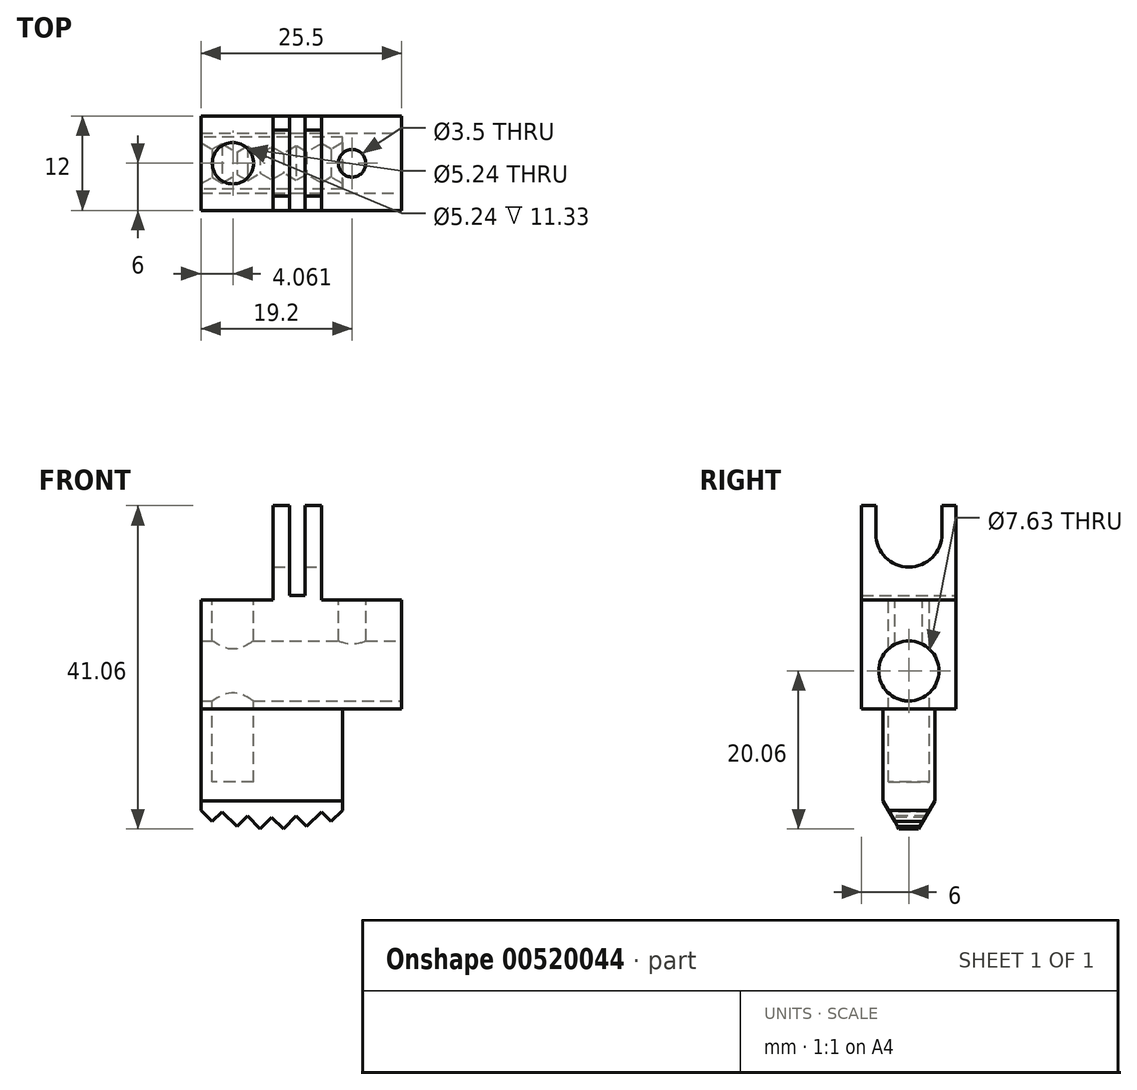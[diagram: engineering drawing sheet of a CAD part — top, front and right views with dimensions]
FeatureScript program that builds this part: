
annotation { "Feature Type Name" : "Feature", "Feature Type Description" : "" }
export const myFeature = defineFeature(function(context is Context, id is Id, definition is map)
    precondition{}
    {
        {
            var Q0;
            Q0=qCreatedBy(makeId("Front.planeOp"),FACE);
            var sketch = newSketch(context, id + "F0", { "sketchPlane" : qUnion([Q0])});
            skLineSegment(sketch, "E0", {"start": v(0, 0) * mm, "end": v(-6, 0) * mm});
            skLineSegment(sketch, "E1", {"start": v(0, 0) * mm, "end": v(0, 5.1) * mm});
            skLineSegment(sketch, "E2", {"start": v(0, 5.1) * mm, "end": v(2.5, 5.1) * mm});
            skLineSegment(sketch, "E3", {"start": v(2.5, 5.1) * mm, "end": v(2.5, 9.7) * mm});
            skLineSegment(sketch, "E4", {"start": v(2.5, 9.7) * mm, "end": v(-0.9, 9.7) * mm});
            skLineSegment(sketch, "E5", {"start": v(-0.9, 9.7) * mm, "end": v(-0.9, 13.7) * mm});
            skLineSegment(sketch, "E6", {"start": v(-0.9, 13.7) * mm, "end": v(-1.6, 13.7) * mm});
            skLineSegment(sketch, "E7", {"start": v(-1.6, 13.7) * mm, "end": v(-1.6, 9.9) * mm});
            skLineSegment(sketch, "E8", {"start": v(-1.6, 9.9) * mm, "end": v(-2.25, 9.9) * mm});
            skLineSegment(sketch, "E9", {"start": v(-2.25, 9.9) * mm, "end": v(-2.25, 13.7) * mm});
            skLineSegment(sketch, "E10", {"start": v(-2.25, 13.7) * mm, "end": v(-2.95, 13.7) * mm});
            skLineSegment(sketch, "E11", {"start": v(-2.95, 13.7) * mm, "end": v(-2.95, 9.7) * mm});
            skLineSegment(sketch, "E12", {"start": v(-2.95, 9.7) * mm, "end": v(-6, 9.7) * mm});
            skLineSegment(sketch, "E13", {"start": v(-6, 9.7) * mm, "end": v(-6, 0) * mm});
            skLineSegment(sketch, "E14", {"start": v(-3, 0) * mm, "end": v(-3, 10) * mm, "construction": true});
            skCircle(sketch, "E15", {"center": v(-3, 10) * mm, "radius": 10 * mm, "construction": true});
            skLineSegment(sketch, "E16", {"start": v(0, 5.1) * mm, "end": v(-6, 5.1) * mm});
            skSolve(sketch);
        }
        {
            var Q0;
            Q0=makeQuery(id+"F0.imprint","IMPRINT",FACE,{"disambiguationData":[TD([[makeQuery(id+"F0.imprint","IMPRINT",EDGE,{"derivedFrom":sQuery(id+"F0.wireOp",EDGE,"E2")}),1.0]])]});
            extrude(context, id + "F1", {"entities" : qUnion([Q0]), "endBound" : BoundingType.SYMMETRIC, "depth" : 4 * mm});
        }
        {
            var Q0;
            {var subQ2=sQuery(id+"F0.wireOp",EDGE,"E0");Q0=makeQuery(id+"F0.imprint","IMPRINT",FACE,{"disambiguationData":[TD([[makeQuery(id+"F0.imprint","IMPRINT",EDGE,{"derivedFrom":subQ2}),-1.0]])]});}
            extrude(context, id + "F2", {"entities" : qUnion([Q0]), "operationType" : NewBodyOperationType.ADD, "endBound" : BoundingType.SYMMETRIC, "depth" : 2.2 * mm});
        }
        {
            var Q0;
            Q0=makeQuery(id+"F1.opExtrude","SWEPT_FACE",FACE,{"disambiguationData":[OSD([sQuery(id+"F0.wireOp",EDGE,"E5")])]});
            var sketch = newSketch(context, id + "F3", { "sketchPlane" : qUnion([Q0])});
            skLineSegment(sketch, "E17", {"start": v(2, 11.1) * mm, "end": v(-2, 11.1) * mm, "construction": true});
            skArc(sketch, "E18", {"start": v(-1.4, 12.5) * mm, "mid": v(0, 11.1) * mm, "end": v(1.4, 12.5) * mm});
            skLineSegment(sketch, "E19", {"start": v(-1.4, 12.5) * mm, "end": v(-1.4, 13.9) * mm});
            skLineSegment(sketch, "E20", {"start": v(-1.4, 13.9) * mm, "end": v(1.4, 13.9) * mm});
            skLineSegment(sketch, "E21", {"start": v(1.4, 13.9) * mm, "end": v(1.4, 12.5) * mm});
            skSolve(sketch);
        }
        {
            var Q0;
            {var subQ5=sQuery(id+"F3.wireOp",EDGE,"E20");Q0=makeQuery(id+"F3.imprint","IMPRINT",FACE,{"disambiguationData":[TD([[makeQuery(id+"F3.imprint","IMPRINT",EDGE,{"derivedFrom":subQ5}),-1.0]])]});}
            var Q1;
            {var subQ5=sQuery(id+"F3.wireOp",EDGE,"E18");Q1=makeQuery(id+"F3.imprint","IMPRINT",FACE,{"disambiguationData":[TD([[makeQuery(id+"F3.imprint","IMPRINT",EDGE,{"derivedFrom":subQ5}),1.0]])]});}
            var Q2;
            Q2=makeQuery(id+"F1.opExtrude","SWEPT_FACE",FACE,{"disambiguationData":[OSD([sQuery(id+"F0.wireOp",EDGE,"E11")])]});
            extrude(context, id + "F4", {"entities" : qUnion([Q0, Q1]), "operationType" : NewBodyOperationType.REMOVE, "endBound" : BoundingType.UP_TO_SURFACE, "oppositeDirection" : true, "endBoundEntityFace" : qUnion([Q2]), "depth" : 2 * mm});
        }
        {
            var Q0;
            Q0=makeQuery(id+"F1.opExtrude","SWEPT_FACE",FACE,{"disambiguationData":[OSD([sQuery(id+"F0.wireOp",EDGE,"E3")])]});
            var sketch = newSketch(context, id + "F5", { "sketchPlane" : qUnion([Q0])});
            skLineSegment(sketch, "E22", {"start": v(0, 9.7) * mm, "end": v(0, 6.7) * mm, "construction": true});
            skCircle(sketch, "E23", {"center": v(0, 6.7) * mm, "radius": 1.27 * mm});
            skSolve(sketch);
        }
        {
            var Q0;
            Q0=makeQuery(id+"F5.imprint","IMPRINT",FACE,{"disambiguationData":[TD([[makeQuery(id+"F5.imprint","IMPRINT",EDGE,{"derivedFrom":sQuery(id+"F5.wireOp",EDGE,"E23")}),1.0]])]});
            extrude(context, id + "F6", {"entities" : qUnion([Q0]), "operationType" : NewBodyOperationType.REMOVE, "oppositeDirection" : true, "depth" : 8.5 * mm});
        }
        {
            var Q0;
            Q0=makeQuery(id+"F1.opExtrude","SWEPT_FACE",FACE,{"disambiguationData":[OSD([sQuery(id+"F0.wireOp",EDGE,"E4")])]});
            var sketch = newSketch(context, id + "F7", { "sketchPlane" : qUnion([Q0])});
            skCircle(sketch, "E24", {"center": v(0.4, 0) * mm, "radius": 0.58 * mm});
            skSolve(sketch);
        }
        {
            var Q0;
            Q0=makeQuery(id+"F7.imprint","IMPRINT",FACE,{"disambiguationData":[TD([[makeQuery(id+"F7.imprint","IMPRINT",EDGE,{"derivedFrom":sQuery(id+"F7.wireOp",EDGE,"E24")}),1.0]])]});
            extrude(context, id + "F8", {"entities" : qUnion([Q0]), "operationType" : NewBodyOperationType.REMOVE, "oppositeDirection" : true, "depth" : 3 * mm});
        }
        {
            var Q0;
            Q0=makeQuery(id+"F1.opExtrude","SWEPT_FACE",FACE,{"disambiguationData":[OSD([sQuery(id+"F0.wireOp",EDGE,"E12")])]});
            var sketch = newSketch(context, id + "F9", { "sketchPlane" : qUnion([Q0])});
            skLineSegment(sketch, "E25", {"start": v(-4.65, 2) * mm, "end": v(-4.65, -2) * mm, "construction": true});
            skCircle(sketch, "E26", {"center": v(-4.65, 0) * mm, "radius": 0.87 * mm});
            skSolve(sketch);
        }
        {
            var Q0;
            Q0=makeQuery(id+"F9.imprint","IMPRINT",FACE,{"disambiguationData":[TD([[makeQuery(id+"F9.imprint","IMPRINT",EDGE,{"derivedFrom":sQuery(id+"F9.wireOp",EDGE,"E26")}),1.0]])]});
            extrude(context, id + "F10", {"entities" : qUnion([Q0]), "operationType" : NewBodyOperationType.REMOVE, "oppositeDirection" : true, "depth" : 7.7 * mm});
        }
        {
            var Q0;
            Q0=makeQuery(id+"F2.opExtrude","CAP_EDGE",EDGE,{"disambiguationData":[OSD([sQuery(id+"F0.wireOp",EDGE,"E0")])],"isStart":false});
            var Q1;
            Q1=makeQuery(id+"F2.opExtrude","CAP_EDGE",EDGE,{"disambiguationData":[OSD([sQuery(id+"F0.wireOp",EDGE,"E0")])],"isStart":true});
            chamfer(context, id + "F11", {"entities" : qUnion([Q0, Q1]), "chamferType" : ChamferType.OFFSET_ANGLE, "width" : 1.2 * mm, "oppositeDirection" : true, "angle" : 30 * degree, "tangentPropagation" : true});
        }
        {
            var Q0;
            Q0=qCreatedBy(makeId("Front.planeOp"),FACE);
            var sketch = newSketch(context, id + "F12", { "sketchPlane" : qUnion([Q0])});
            skCircle(sketch, "E27", {"center": v(-3, 10) * mm, "radius": 10 * mm, "construction": true});
            skPoint(sketch, "E28", {"position": v(-3, 0) * mm});
            skCircle(sketch, "E29", {"center": v(-3, 10) * mm, "radius": 9.5 * mm, "construction": true});
            skLineSegment(sketch, "E30", {"start": v(-3, 0.5) * mm, "end": v(-3.49, 0.01) * mm});
            skLineSegment(sketch, "E31", {"start": v(-3, 0.5) * mm, "end": v(-2.51, 0.01) * mm});
            skLineSegment(sketch, "E32", {"start": v(-3.49, 0.01) * mm, "end": v(-4.03, 0.56) * mm});
            skLineSegment(sketch, "E33", {"start": v(-4.03, 0.56) * mm, "end": v(-4.48, 0.1) * mm});
            skLineSegment(sketch, "E34", {"start": v(-4.48, 0.1) * mm, "end": v(-5.1, 0.74) * mm});
            skLineSegment(sketch, "E35", {"start": v(-5.1, 0.74) * mm, "end": v(-5.52, 0.32) * mm});
            skLineSegment(sketch, "E36", {"start": v(-5.52, 0.32) * mm, "end": v(-6, 0.8) * mm});
            skLineSegment(sketch, "E37", {"start": v(-6, 0.8) * mm, "end": v(-6, 0) * mm});
            skLineSegment(sketch, "E38", {"start": v(-6, 0) * mm, "end": v(0, 0) * mm});
            skLineSegment(sketch, "E39", {"start": v(0, 0) * mm, "end": v(0, 0.8) * mm});
            skLineSegment(sketch, "E40", {"start": v(-2.51, 0.01) * mm, "end": v(-1.97, 0.56) * mm});
            skLineSegment(sketch, "E41", {"start": v(-1.97, 0.56) * mm, "end": v(-1.52, 0.1) * mm});
            skLineSegment(sketch, "E42", {"start": v(-1.52, 0.1) * mm, "end": v(-0.9, 0.74) * mm});
            skLineSegment(sketch, "E43", {"start": v(-0.9, 0.74) * mm, "end": v(-0.48, 0.32) * mm});
            skLineSegment(sketch, "E44", {"start": v(-0.48, 0.32) * mm, "end": v(0, 0.8) * mm});
            skSolve(sketch);
        }
        {
            var Q0;
            Q0=makeQuery(id+"F12.imprint","IMPRINT",FACE,{"disambiguationData":[TD([[makeQuery(id+"F12.imprint","IMPRINT",EDGE,{"derivedFrom":sQuery(id+"F12.wireOp",EDGE,"E30")}),1.0]])]});
            extrude(context, id + "F13", {"entities" : qUnion([Q0]), "operationType" : NewBodyOperationType.REMOVE, "endBound" : BoundingType.SYMMETRIC, "oppositeDirection" : true, "depth" : 25 * mm});
        }
        {
            var Q0;
            Q0=makeQuery(id+"F1.opExtrude","SWEPT_BODY",BODY,{"disambiguationData":[OSD([sQuery(id+"F0.wireOp",EDGE,"E2"),sQuery(id+"F0.wireOp",EDGE,"E3"),sQuery(id+"F0.wireOp",EDGE,"E4"),sQuery(id+"F0.wireOp",EDGE,"E5"),sQuery(id+"F0.wireOp",EDGE,"E6"),sQuery(id+"F0.wireOp",EDGE,"E7"),sQuery(id+"F0.wireOp",EDGE,"E8"),sQuery(id+"F0.wireOp",EDGE,"E9"),sQuery(id+"F0.wireOp",EDGE,"E10"),sQuery(id+"F0.wireOp",EDGE,"E11"),sQuery(id+"F0.wireOp",EDGE,"E12"),sQuery(id+"F0.wireOp",EDGE,"E13"),sQuery(id+"F0.wireOp",EDGE,"E16")])]});
            var Q1;
            Q1=qCreatedBy(makeId("Origin.pointOp"),VERTEX);
            transform(context, id + "F14", {"entities" : qUnion([Q0]), "transformType" : TransformType.SCALE_UNIFORMLY, "scale" : 3, "makeCopy" : false, "scalePoint" : qUnion([Q1])});
        }
    });
